# Revit family: PRESTO XT-LM PALANCA con llaves de paso
name_source: partatom
category: Aparatos sanitarios
revit_build: Autodesk Revit 2015 (Build: 20140223_1515(x64)
units: mm (PartAtom-declared; Revit-internal decimal feet)

## types (1)
- 26242
    Accionamiento = Por pulsador
    CAUDAL = 6 L/Min
    CIERRE = Automático en 15 seg.
    Comentarios de tipo = Cuerpo y pulsador en latón cromado, piezas interiores en materiales resistentes a la corrosión y a las incrustaciones calcáreas
◦Suministrado con brida, latiguillos flexible en acero inoxidable de ½” y 350 mm de longitud y juntas.
Válvulas antirretorno que impiden la intercomunicación del agua fría y caliente
    Conexión AC = Sí
    Conexión AF = Sí
    Código de montaje = C1030220
    Descripción = Grifo temporizado mezclador para instalación sobre repisa con cuerpo de latón cromado.
    ENTRADA = Latiguillos flexibles de 1/2''
    Elevación por defecto = 1219 mm
    Fabricante = PRESTO IBÉRICA
    Imagen de tipo = <Ninguno>
    Material = LATON CROMADO
    Modelo = PRESTO XT LM PALANCA
    PESO BRUTO = 1.118 Kg
    Presión Máxima = 5 bar
    REFERENCIA = 26242
    TIPO DE AGUA = Fria/Caliente
    Teléfono = (+34) 915 782 575
    URL = http://www.prestoiberica.com
